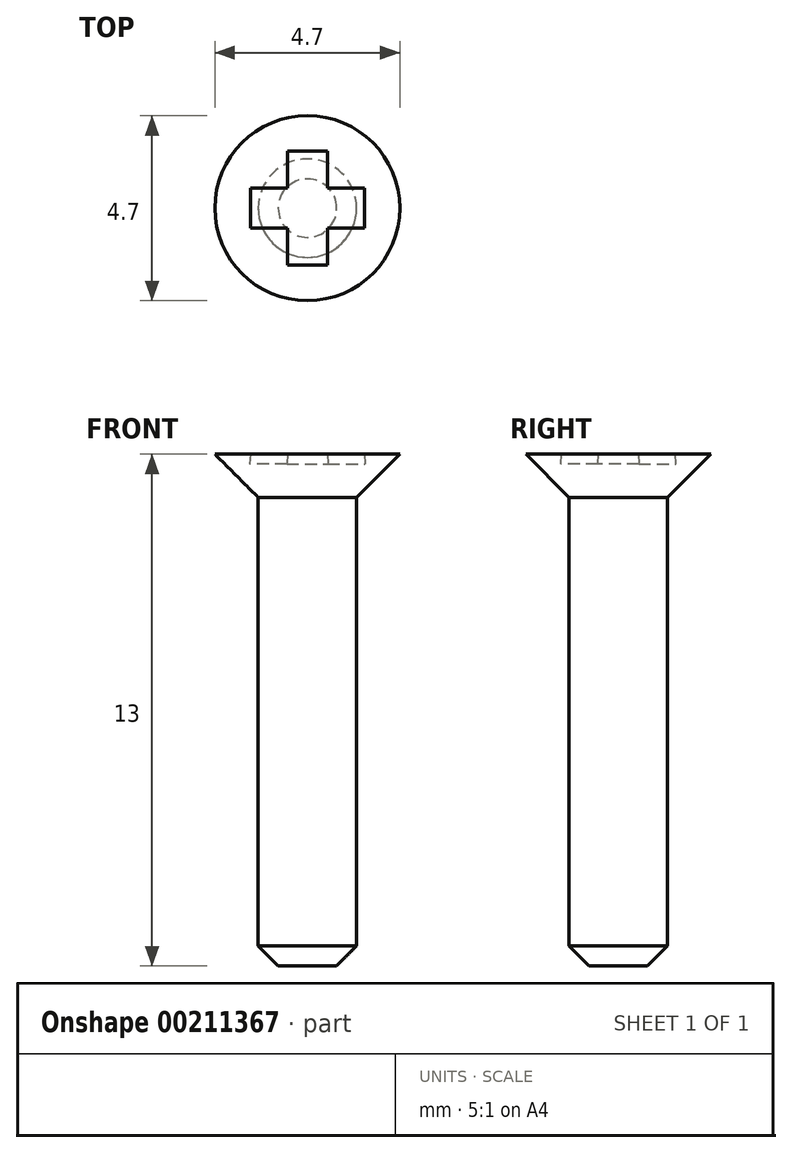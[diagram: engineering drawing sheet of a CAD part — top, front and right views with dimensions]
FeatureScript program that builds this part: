
annotation { "Feature Type Name" : "Feature", "Feature Type Description" : "" }
export const myFeature = defineFeature(function(context is Context, id is Id, definition is map)
    precondition{}
    {
        {
            var Q0;
            Q0=qCreatedBy(makeId("Front.planeOp"),FACE);
            var sketch = newSketch(context, id + "F0", { "sketchPlane" : qUnion([Q0])});
            skLineSegment(sketch, "E0", {"start": v(0, 0) * mm, "end": v(0, 13) * mm});
            skLineSegment(sketch, "E1", {"start": v(0, 13) * mm, "end": v(2.35, 13) * mm});
            skLineSegment(sketch, "E2", {"start": v(2.35, 13) * mm, "end": v(1.25, 11.9) * mm});
            skLineSegment(sketch, "E3", {"start": v(1.25, 11.9) * mm, "end": v(1.25, 0) * mm});
            skLineSegment(sketch, "E4", {"start": v(1.25, 0) * mm, "end": v(0, 0) * mm});
            skSolve(sketch);
        }
        {
            var Q0;
            Q0=qSketchRegion(id+"F0",true);
            var Q1;
            Q1=qConstructionFilter(qBodyType(qCreatedBy(id+"F0",EDGE),BodyType.WIRE),ConstructionObject.NO);
            var Q2;
            Q2=sQuery(id+"F0.wireOp",EDGE,"E0");
            revolve(context, id + "F1", {"entities" : qUnion([Q0]), "surfaceEntities" : qUnion([Q1]), "axis" : qUnion([Q2]), "revolveType" : RevolveType.FULL});
        }
        {
            var Q0;
            Q0=makeQuery(id+"F1.opRevolve","SWEPT_FACE",FACE,{"disambiguationData":[OSD([sQuery(id+"F0.wireOp",EDGE,"E1")])]});
            var sketch = newSketch(context, id + "F2", { "sketchPlane" : qUnion([Q0])});
            skLineSegment(sketch, "E5.bottom", {"start": v(-1.45, 0.5) * mm, "end": v(1.45, 0.5) * mm});
            skLineSegment(sketch, "E5.top", {"start": v(-1.45, -0.5) * mm, "end": v(1.45, -0.5) * mm});
            skLineSegment(sketch, "E5.left", {"start": v(-1.45, 0.5) * mm, "end": v(-1.45, -0.5) * mm});
            skLineSegment(sketch, "E5.right", {"start": v(1.45, 0.5) * mm, "end": v(1.45, -0.5) * mm});
            skLineSegment(sketch, "E6.bottom", {"start": v(-0.5, 1.45) * mm, "end": v(0.5, 1.45) * mm});
            skLineSegment(sketch, "E6.top", {"start": v(-0.5, -1.45) * mm, "end": v(0.5, -1.45) * mm});
            skLineSegment(sketch, "E6.left", {"start": v(-0.5, 1.45) * mm, "end": v(-0.5, -1.45) * mm});
            skLineSegment(sketch, "E6.right", {"start": v(0.5, 1.45) * mm, "end": v(0.5, -1.45) * mm});
            skLineSegment(sketch, "E7", {"start": v(0, 1.45) * mm, "end": v(0, -1.45) * mm});
            skLineSegment(sketch, "E8", {"start": v(-1.45, 0) * mm, "end": v(1.45, 0) * mm});
            skLineSegment(sketch, "E9", {"start": v(-1.45, 0.5) * mm, "end": v(0, 0) * mm});
            skLineSegment(sketch, "E10", {"start": v(0, 0) * mm, "end": v(0.5, 1.45) * mm});
            skLineSegment(sketch, "E11", {"start": v(0, 0) * mm, "end": v(1.45, -0.5) * mm});
            skLineSegment(sketch, "E12", {"start": v(0, 0) * mm, "end": v(-0.5, -1.45) * mm});
            skSolve(sketch);
        }
        {
            var Q0;
            Q0=qSketchRegion(id+"F2",true);
            var Q1;
            {var subQ0=sQuery(id+"F2.wireOp",EDGE,"E7");var subQ1=sQuery(id+"F2.wireOp",EDGE,"E5.bottom");var subQ2=makeQuery(id+"F2.imprint","INTERSECT",VERTEX,{"derivedFrom":[subQ1,subQ0]});Q1=makeQuery(id+"F2.imprint","IMPRINT",FACE,{"disambiguationData":[TD([[makeQuery(id+"F2.imprint","IMPRINT",EDGE,{"disambiguationData":[TD([[subQ2,-1.0]])],"derivedFrom":subQ1}),-1.0]])]});}
            var Q2;
            {var subQ0=sQuery(id+"F2.wireOp",EDGE,"E8");var subQ1=sQuery(id+"F2.wireOp",EDGE,"E6.right");var subQ2=makeQuery(id+"F2.imprint","INTERSECT",VERTEX,{"derivedFrom":[subQ1,subQ0]});Q2=makeQuery(id+"F2.imprint","IMPRINT",FACE,{"disambiguationData":[TD([[makeQuery(id+"F2.imprint","IMPRINT",EDGE,{"disambiguationData":[TD([[subQ2,-1.0]])],"derivedFrom":subQ1}),-1.0]])]});}
            var Q3;
            {var subQ0=sQuery(id+"F2.wireOp",EDGE,"E12");var subQ1=sQuery(id+"F2.wireOp",EDGE,"E5.top");var subQ2=makeQuery(id+"F2.imprint","INTERSECT",VERTEX,{"derivedFrom":[subQ1,subQ0]});Q3=makeQuery(id+"F2.imprint","IMPRINT",FACE,{"disambiguationData":[TD([[makeQuery(id+"F2.imprint","IMPRINT",EDGE,{"disambiguationData":[TD([[subQ2,-1.0]])],"derivedFrom":subQ1}),1.0]])]});}
            var Q4;
            {var subQ0=sQuery(id+"F2.wireOp",EDGE,"E9");var subQ1=sQuery(id+"F2.wireOp",EDGE,"E6.left");var subQ2=makeQuery(id+"F2.imprint","INTERSECT",VERTEX,{"derivedFrom":[subQ1,subQ0]});Q4=makeQuery(id+"F2.imprint","IMPRINT",FACE,{"disambiguationData":[TD([[makeQuery(id+"F2.imprint","IMPRINT",EDGE,{"disambiguationData":[TD([[subQ2,-1.0]])],"derivedFrom":subQ1}),1.0]])]});}
            extrude(context, id + "F3", {"entities" : qUnion([Q0, Q1, Q2, Q3, Q4]), "operationType" : NewBodyOperationType.REMOVE, "oppositeDirection" : true, "depth" : 0.25 * mm, "hasDraft" : true, "draftAngle" : 3 * degree});
        }
        {
            var Q0;
            Q0=makeQuery(id+"F1.opRevolve","SWEPT_EDGE",EDGE,{"disambiguationData":[OSD([sQuery(id+"F0.wireOp",EDGE,"E3"),sQuery(id+"F0.wireOp",EDGE,"E4")])]});
            chamfer(context, id + "F4", {"entities" : qUnion([Q0]), "width" : 0.5 * mm, "tangentPropagation" : true});
        }
    });
